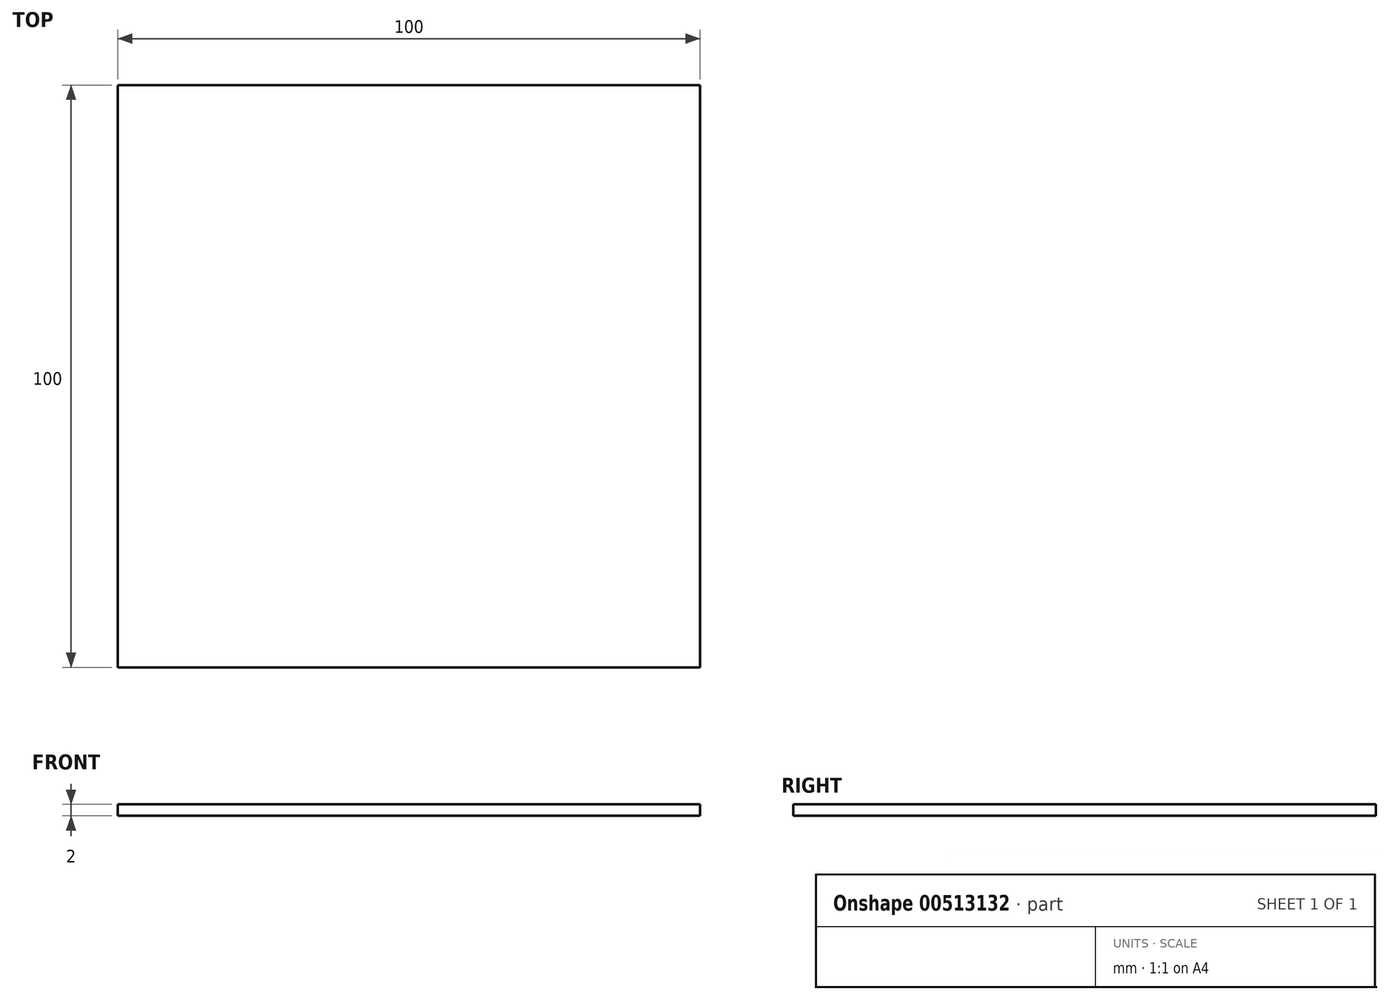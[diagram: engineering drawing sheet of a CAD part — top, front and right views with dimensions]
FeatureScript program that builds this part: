
annotation { "Feature Type Name" : "Feature", "Feature Type Description" : "" }
export const myFeature = defineFeature(function(context is Context, id is Id, definition is map)
    precondition{}
    {
        {
            var Q0;
            Q0=qCreatedBy(makeId("Top.planeOp"),FACE);
            var sketch = newSketch(context, id + "F0", { "sketchPlane" : qUnion([Q0])});
            skLineSegment(sketch, "E0.bottom", {"start": v(-86.28, 71.5) * mm, "end": v(13.72, 71.5) * mm});
            skLineSegment(sketch, "E0.top", {"start": v(-86.28, -28.5) * mm, "end": v(13.72, -28.5) * mm});
            skLineSegment(sketch, "E0.left", {"start": v(-86.28, 71.5) * mm, "end": v(-86.28, -28.5) * mm});
            skLineSegment(sketch, "E0.right", {"start": v(13.72, 71.5) * mm, "end": v(13.72, -28.5) * mm});
            skSolve(sketch);
        }
        {
            var Q0;
            Q0=makeQuery(id+"F0.imprint","IMPRINT",FACE,{"disambiguationData":[TD([[makeQuery(id+"F0.imprint","IMPRINT",EDGE,{"derivedFrom":sQuery(id+"F0.wireOp",EDGE,"E0.bottom")}),-1.0]])]});
            extrude(context, id + "F1", {"entities" : qUnion([Q0]), "depth" : 2 * mm});
        }
    });
